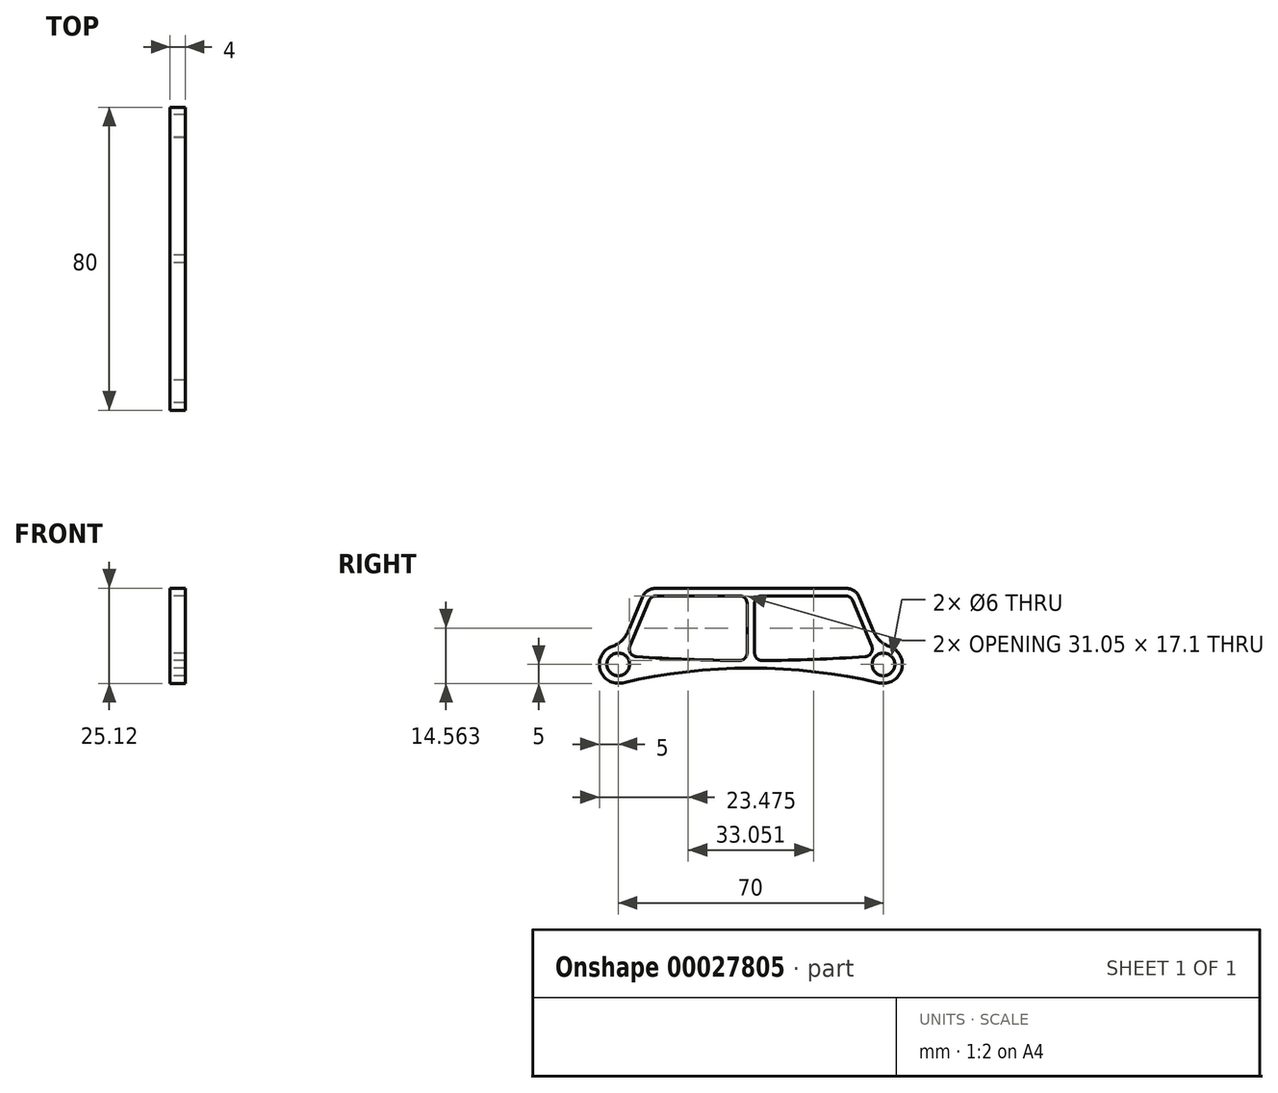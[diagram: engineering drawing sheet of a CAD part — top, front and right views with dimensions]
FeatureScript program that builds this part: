
annotation { "Feature Type Name" : "Feature", "Feature Type Description" : "" }
export const myFeature = defineFeature(function(context is Context, id is Id, definition is map)
    precondition{}
    {
        {
            var Q0;
            Q0=qCreatedBy(makeId("Right.planeOp"),FACE);
            var sketch = newSketch(context, id + "F0", { "sketchPlane" : qUnion([Q0])});
            skCircle(sketch, "E0", {"center": v(0, 0) * mm, "radius": 3 * mm});
            skArc(sketch, "E1", {"start": v(-1.6, 4.74) * mm, "mid": v(-4.81, -1.36) * mm, "end": v(1.13, -4.87) * mm});
            skPoint(sketch, "E2.visualSharp", {"position": v(70, 20) * mm});
            skPoint(sketch, "E3.center.orphan", {"position": v(70, 0) * mm});
            skLineSegment(sketch, "E4", {"start": v(35, -1) * mm, "end": v(35, -1) * mm});
            skPoint(sketch, "E5.visualSharp", {"position": v(1.4, 4.8) * mm});
            skArc(sketch, "E6", {"start": v(35, -1) * mm, "mid": v(17.95, -1.97) * mm, "end": v(1.13, -4.87) * mm});
            skLineSegment(sketch, "E7", {"start": v(0.97, 2.32) * mm, "end": v(7.23, 17.27) * mm, "construction": true});
            skLineSegment(sketch, "E8", {"start": v(10, 19.12) * mm, "end": v(35, 19.12) * mm, "construction": true});
            skPoint(sketch, "E9.visualSharp", {"position": v(8, 19.12) * mm});
            skArc(sketch, "E9.filletArc", {"start": v(10, 19.12) * mm, "mid": v(8.34, 18.61) * mm, "end": v(7.23, 17.27) * mm, "construction": true});
            skLineSegment(sketch, "E10.0", {"start": v(10, 18.12) * mm, "end": v(32, 18.12) * mm});
            skLineSegment(sketch, "E10.1", {"start": v(3.1, 4.81) * mm, "end": v(8.16, 16.89) * mm});
            skLineSegment(sketch, "E11.0", {"start": v(10, 20.12) * mm, "end": v(35, 20.12) * mm});
            skArc(sketch, "E11.1", {"start": v(10, 20.12) * mm, "mid": v(7.78, 19.45) * mm, "end": v(6.31, 17.66) * mm});
            skLineSegment(sketch, "E11.2", {"start": v(2.5, 8.54) * mm, "end": v(6.31, 17.66) * mm});
            skPoint(sketch, "E12.visualSharp", {"position": v(8.67, 18.12) * mm});
            skArc(sketch, "E12.filletArc", {"start": v(10, 18.12) * mm, "mid": v(8.9, 17.78) * mm, "end": v(8.16, 16.89) * mm});
            skArc(sketch, "E13.trimOffspring", {"start": v(4.8, 2.04) * mm, "mid": v(18.39, 1.32) * mm, "end": v(31.99, 1.01) * mm});
            skArc(sketch, "E14", {"start": v(-1.6, 4.74) * mm, "mid": v(0.86, 6.2) * mm, "end": v(2.5, 8.54) * mm});
            skPoint(sketch, "E15.visualSharp", {"position": v(2.02, 2.24) * mm});
            skArc(sketch, "E15.filletArc", {"start": v(3.1, 4.81) * mm, "mid": v(3.24, 2.99) * mm, "end": v(4.8, 2.04) * mm});
            skLineSegment(sketch, "E16", {"start": v(34, 16.12) * mm, "end": v(34, 3.01) * mm});
            skPoint(sketch, "E17.orphan", {"position": v(35, 1) * mm});
            skPoint(sketch, "E18.visualSharp", {"position": v(34, 18.12) * mm});
            skArc(sketch, "E18.filletArc", {"start": v(34, 16.12) * mm, "mid": v(33.41, 17.53) * mm, "end": v(32, 18.12) * mm});
            skPoint(sketch, "E19.visualSharp", {"position": v(34, 1) * mm});
            skArc(sketch, "E19.filletArc", {"start": v(31.99, 1.01) * mm, "mid": v(33.4, 1.6) * mm, "end": v(34, 3.01) * mm});
            skArc(sketch, "E20.MirrorCS", {"start": v(60, 18.12) * mm, "mid": v(61.1, 17.78) * mm, "end": v(61.84, 16.89) * mm});
            skLineSegment(sketch, "E21.MirrorCS", {"start": v(67.5, 8.54) * mm, "end": v(63.69, 17.66) * mm});
            skLineSegment(sketch, "E22.MirrorCS", {"start": v(36, 16.12) * mm, "end": v(36, 3.01) * mm});
            skArc(sketch, "E23.MirrorCS", {"start": v(38.01, 1.01) * mm, "mid": v(36.6, 1.6) * mm, "end": v(36, 3.01) * mm});
            skPoint(sketch, "E24.MirrorP", {"position": v(36, 1) * mm});
            skArc(sketch, "E25.MirrorCS", {"start": v(36, 16.12) * mm, "mid": v(36.59, 17.53) * mm, "end": v(38, 18.12) * mm});
            skPoint(sketch, "E26.MirrorP", {"position": v(62, 19.12) * mm});
            skArc(sketch, "E27.MirrorCS", {"start": v(71.6, 4.74) * mm, "mid": v(69.14, 6.2) * mm, "end": v(67.5, 8.54) * mm});
            skArc(sketch, "E28.MirrorCS", {"start": v(65.2, 2.04) * mm, "mid": v(51.61, 1.32) * mm, "end": v(38.01, 1.01) * mm});
            skPoint(sketch, "E29.MirrorP", {"position": v(68.6, 4.8) * mm});
            skCircle(sketch, "E30.MirrorC", {"center": v(70, 0) * mm, "radius": 3 * mm});
            skPoint(sketch, "E31.MirrorP", {"position": v(67.98, 2.24) * mm});
            skArc(sketch, "E32.MirrorCS", {"start": v(60, 20.12) * mm, "mid": v(62.22, 19.45) * mm, "end": v(63.69, 17.66) * mm});
            skPoint(sketch, "E33.MirrorP", {"position": v(36, 18.12) * mm});
            skPoint(sketch, "E34.MirrorP", {"position": v(61.33, 18.12) * mm});
            skLineSegment(sketch, "E35.MirrorCS", {"start": v(60, 20.12) * mm, "end": v(35, 20.12) * mm});
            skLineSegment(sketch, "E36.MirrorCS", {"start": v(60, 18.12) * mm, "end": v(38, 18.12) * mm});
            skArc(sketch, "E37.MirrorCS", {"start": v(66.9, 4.81) * mm, "mid": v(66.76, 2.99) * mm, "end": v(65.2, 2.04) * mm});
            skArc(sketch, "E38.MirrorCS", {"start": v(35, -1) * mm, "mid": v(52.05, -1.97) * mm, "end": v(68.87, -4.87) * mm});
            skLineSegment(sketch, "E39.MirrorCS", {"start": v(66.9, 4.81) * mm, "end": v(61.84, 16.89) * mm});
            skArc(sketch, "E40.MirrorCS", {"start": v(71.6, 4.74) * mm, "mid": v(74.81, -1.36) * mm, "end": v(68.87, -4.87) * mm});
            skSolve(sketch);
        }
        {
            var Q0;
            Q0=makeQuery(id+"F0.imprint","IMPRINT",FACE,{"disambiguationData":[TD([[makeQuery(id+"F0.imprint","IMPRINT",EDGE,{"derivedFrom":sQuery(id+"F0.wireOp",EDGE,"E0")}),-1.0]])]});
            extrude(context, id + "F1", {"entities" : qUnion([Q0]), "depth" : 4 * mm});
        }
    });
